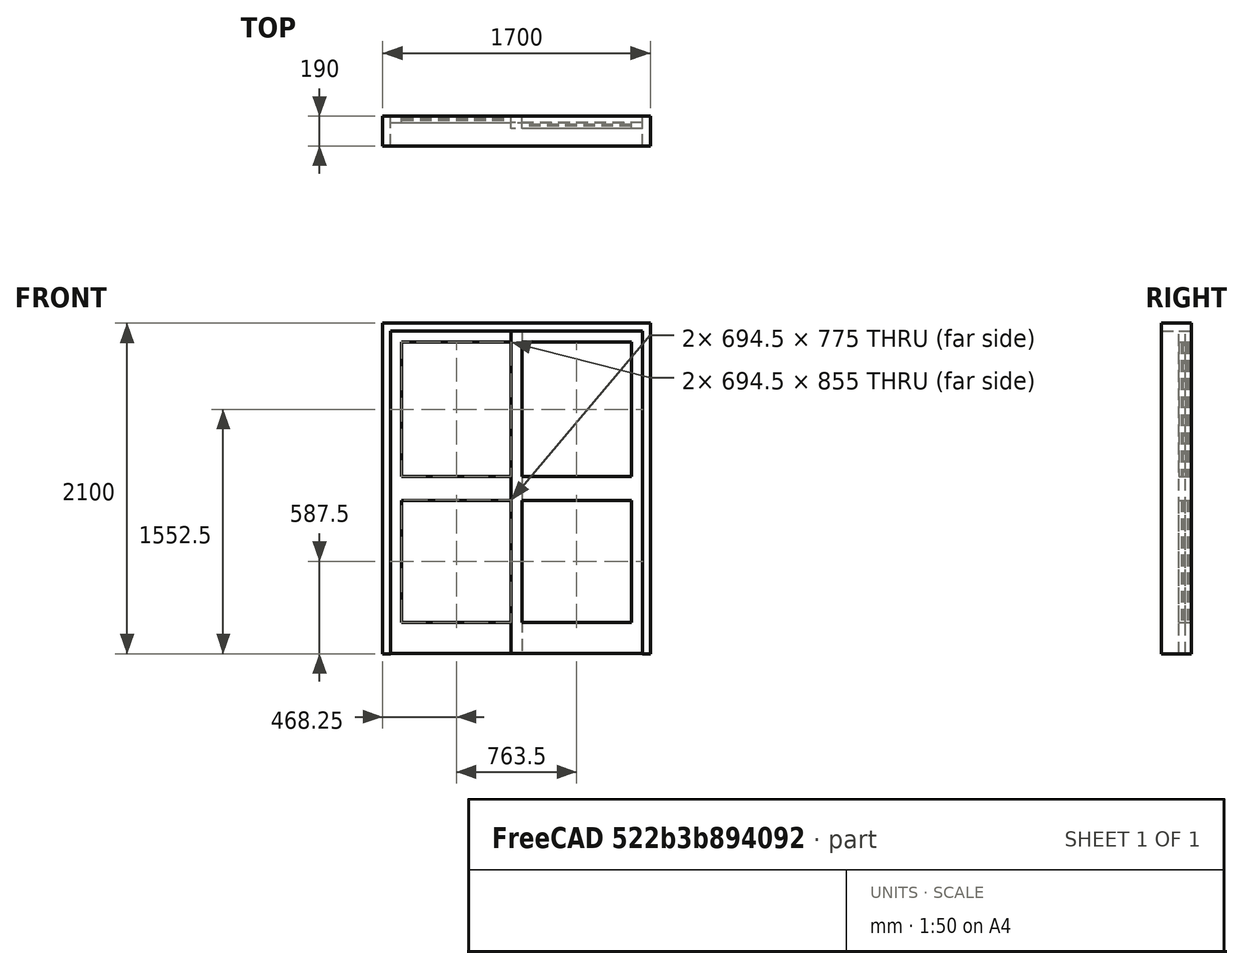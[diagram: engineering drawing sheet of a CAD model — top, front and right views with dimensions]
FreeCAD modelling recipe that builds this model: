
FCSTD DOCUMENT  (FreeCAD 0.16R6704 (Git))
Label: Slinding door 2 sheets with glass
License: CreativeCommons Attribution
LicenseURL: http://creativecommons.org/licenses/by/4.0/
objects: Sketcher::SketchObject×1, Part::FeaturePython×1
note: 2 computed .brp shape members not serialized (recipe doc carries the construction recipe); baked Part::Feature solids carry a one-line shape summary decoded from their .brp

FEATURE [Sketcher::SketchObject] Sketch176  label="Sketch"
  Placement = pos=(0,0,0) rot=(1,0,0;1.5708rad)
  sketch-geometry (34):
    g0: LineSegment StartX=0 StartY=0 StartZ=0 EndX=1700 EndY=0 EndZ=0
    g1: LineSegment StartX=1700 StartY=0 StartZ=0 EndX=1700 EndY=2100 EndZ=0
    g2: LineSegment StartX=1700 StartY=2100 StartZ=0 EndX=0 EndY=2100 EndZ=0
    g3: LineSegment StartX=0 StartY=2100 StartZ=0 EndX=0 EndY=0 EndZ=0
    g4: LineSegment StartX=50 StartY=0 StartZ=0 EndX=1650 EndY=0 EndZ=0
    g5: LineSegment StartX=1650 StartY=0 StartZ=0 EndX=1650 EndY=2050 EndZ=0
    g6: LineSegment StartX=1650 StartY=2050 StartZ=0 EndX=50 EndY=2050 EndZ=0
    g7: LineSegment StartX=50 StartY=2050 StartZ=0 EndX=50 EndY=0 EndZ=0
    g8: LineSegment StartX=121 StartY=1980 StartZ=0 EndX=815.5 EndY=1980 EndZ=0
    g9: LineSegment StartX=815.5 StartY=1980 StartZ=0 EndX=815.5 EndY=1125 EndZ=0
    g10: LineSegment StartX=815.5 StartY=1125 StartZ=0 EndX=121 EndY=1125 EndZ=0
    g11: LineSegment StartX=121 StartY=1125 StartZ=0 EndX=121 EndY=1980 EndZ=0
    g12: LineSegment StartX=121 StartY=975 StartZ=0 EndX=815.5 EndY=975 EndZ=0
    g13: LineSegment StartX=815.5 StartY=975 StartZ=0 EndX=815.5 EndY=200 EndZ=0
    g14: LineSegment StartX=815.5 StartY=200 StartZ=0 EndX=121 EndY=200 EndZ=0
    g15: LineSegment StartX=121 StartY=200 StartZ=0 EndX=121 EndY=975 EndZ=0
    g16: LineSegment [constr] StartX=-278 StartY=1050 StartZ=0 EndX=2205 EndY=1050 EndZ=0
    g17: LineSegment StartX=51 StartY=2049 StartZ=0 EndX=885.5 EndY=2049 EndZ=0
    g18: LineSegment StartX=885.5 StartY=2049 StartZ=0 EndX=885.5 EndY=1 EndZ=0
    g19: LineSegment StartX=885.5 StartY=1 StartZ=0 EndX=51 EndY=1 EndZ=0
    g20: LineSegment StartX=51 StartY=1 StartZ=0 EndX=51 EndY=2049 EndZ=0
    g21: LineSegment [constr] StartX=850 StartY=2319.78 StartZ=0 EndX=850 EndY=-188.278 EndZ=0
    g22: LineSegment StartX=1579 StartY=1980 StartZ=0 EndX=884.5 EndY=1980 EndZ=0
    g23: LineSegment StartX=884.5 StartY=1980 StartZ=0 EndX=884.5 EndY=1125 EndZ=0
    g24: LineSegment StartX=884.5 StartY=1125 StartZ=0 EndX=1579 EndY=1125 EndZ=0
    g25: LineSegment StartX=1579 StartY=1125 StartZ=0 EndX=1579 EndY=1980 EndZ=0
    g26: LineSegment StartX=1579 StartY=975 StartZ=0 EndX=884.5 EndY=975 EndZ=0
    g27: LineSegment StartX=884.5 StartY=975 StartZ=0 EndX=884.5 EndY=200 EndZ=0
    g28: LineSegment StartX=884.5 StartY=200 StartZ=0 EndX=1579 EndY=200 EndZ=0
    g29: LineSegment StartX=1579 StartY=200 StartZ=0 EndX=1579 EndY=975 EndZ=0
    g30: LineSegment StartX=1649 StartY=2049 StartZ=0 EndX=814.5 EndY=2049 EndZ=0
    g31: LineSegment StartX=814.5 StartY=2049 StartZ=0 EndX=814.5 EndY=1 EndZ=0
    g32: LineSegment StartX=814.5 StartY=1 StartZ=0 EndX=1649 EndY=1 EndZ=0
    g33: LineSegment StartX=1649 StartY=1 StartZ=0 EndX=1649 EndY=2049 EndZ=0
  constraints (99):
    c: Coincident(g0,g1)
    c: Coincident(g1,g2)
    c: Coincident(g2,g3)
    c: Coincident(g3,g0)
    c: Horizontal(g0)
    c: Horizontal(g2)
    c: Vertical(g1)
    c: Vertical(g3)
    c: Coincident(g4,g5)
    c: Coincident(g5,g6)
    c: Coincident(g6,g7)
    c: Coincident(g7,g4)
    c: Horizontal(g4)
    c: Horizontal(g6)
    c: Vertical(g5)
    c: Vertical(g7)
    c: DistanceY(g1) = 2100  'Altura do vão'
    c: DistanceX(g0) = 1700  'Largura do vão'
    c: DistanceY(g6,g2) = 50  'Batente horizontal'
    c: DistanceX(g2,g6) = 50  'Batente vertical 1'
    c: DistanceX(g4,g0) = 50  'Batente vertical 2'
    c: DistanceY(g0,g4) = 0
    c: Coincident(g0,g-1)
    c: Coincident(g8,g9)
    c: Coincident(g9,g10)
    c: Coincident(g10,g11)
    c: Coincident(g11,g8)
    c: Horizontal(g8)
    c: Horizontal(g10)
    c: Vertical(g9)
    c: Vertical(g11)
    c: Coincident(g12,g13)
    c: Coincident(g13,g14)
    c: Coincident(g14,g15)
    c: Coincident(g15,g12)
    c: Horizontal(g12)
    c: Horizontal(g14)
    c: Vertical(g13)
    c: Vertical(g15)
    c: DistanceX(g10,g12) = 0
    c: DistanceX(g9,g12) = 0
    c: DistanceY(g12,g10) = 150  'Montante intermediário portas'
    c: DistanceY(g8,g6) = 70  'Altura montante horizontal superior portas'
    c: DistanceY(g-1,g14) = 200  'Montante inferior portas'
    c: Horizontal(g16)
    c: Symmetric(g10,g12,g16)
    c: DistanceY(g-1,g16) = 1050  'Altura montante intermediário portas (eixo) ao chão'
    c: Coincident(g17,g18)
    c: Coincident(g18,g19)
    c: Coincident(g19,g20)
    c: Horizontal(g17)
    c: Horizontal(g19)
    c: Vertical(g18)
    c: Vertical(g20)
    c: DistanceY(g4,g18) = 1
    c: DistanceX(g6,g17) = 1
    c: DistanceY(g17,g6) = 1  'Constraint59'
    c: DistanceX(g8,g17) = 70  'Largura montante vertical 2 porta 1'
    c: DistanceX(g17,g8) = 70  'Largura montante porta 2'
    c: Vertical(g21)
    c: Symmetric(g2,g1,g21)
    c: Coincident(g22,g23)
    c: Coincident(g23,g24)
    c: Coincident(g24,g25)
    c: Coincident(g25,g22)
    c: Horizontal(g22)
    c: Horizontal(g24)
    c: Vertical(g23)
    c: Vertical(g25)
    c: Coincident(g26,g27)
    c: Coincident(g27,g28)
    c: Coincident(g28,g29)
    c: Coincident(g29,g26)
    c: Horizontal(g26)
    c: Horizontal(g28)
    c: Vertical(g27)
    c: Vertical(g29)
    c: Coincident(g30,g31)
    c: Coincident(g31,g32)
    c: Coincident(g32,g33)
    c: Horizontal(g30)
    c: Horizontal(g32)
    c: Vertical(g31)
    c: Vertical(g33)
    c: DistanceX(g30,g5) = 1
    c: DistanceY(g30,g5) = 1
    c: DistanceY(g8,g22) = 0
    c: DistanceY(g9,g23) = 0
    c: DistanceY(g26,g12) = 0
    c: DistanceX(g24,g26) = 0
    c: Coincident(g30,g33)
    c: DistanceX(g30,g22) = 70  'Largura montante vertical 1 porta 2'
    c: DistanceX(g22,g30) = 70  'Largura montante vertical 2 porta 2'
    c: DistanceX(g23,g26) = 0  'Constraint95'
    c: DistanceX(g30,g8) = 1
    c: DistanceY(g27,g13) = 0
    c: Symmetric(g8,g22,g21)
    c: DistanceY(g31,g18) = 0
    c: Coincident(g20,g17)
FEATURE [Part::FeaturePython] Window109  label="Slinding door 2 sheets with glass "  # WARN: FeaturePython — macro-defined, semantics opaque (R4)
  Base = -> Sketch176
  Height = 2100
  HoleDepth = 0
  MoveWithHost = true
  Normal = (0,1,0)
  Preset = 6
  Role = 1
  Width = 900
  WindowParts = BATENTE | Frame | Wire0,Wire1 | 190.0 | 0.0 | PORTA 1 | Frame | Wire2,Wire3,Wire4 | 40.0 | 150.0 | PORTA 2 | Frame | Wire5,Wire6,Wire7 | 40.0 | 110.0 | VIDRO SUPERIOR 1 | Glass panel | Wire2 | 10.0 | 165.0 | VIDRO SUPERIOR 2 | Glass panel | Wire5 | 10.0 | 125.0 | VIDRO INFERIOR 1 | Glass panel | Wire3 | 10.0 | 165.0 | VIDRO INFERIOR 2 | Glass panel | Wire6 | 10.0 | 125.0
